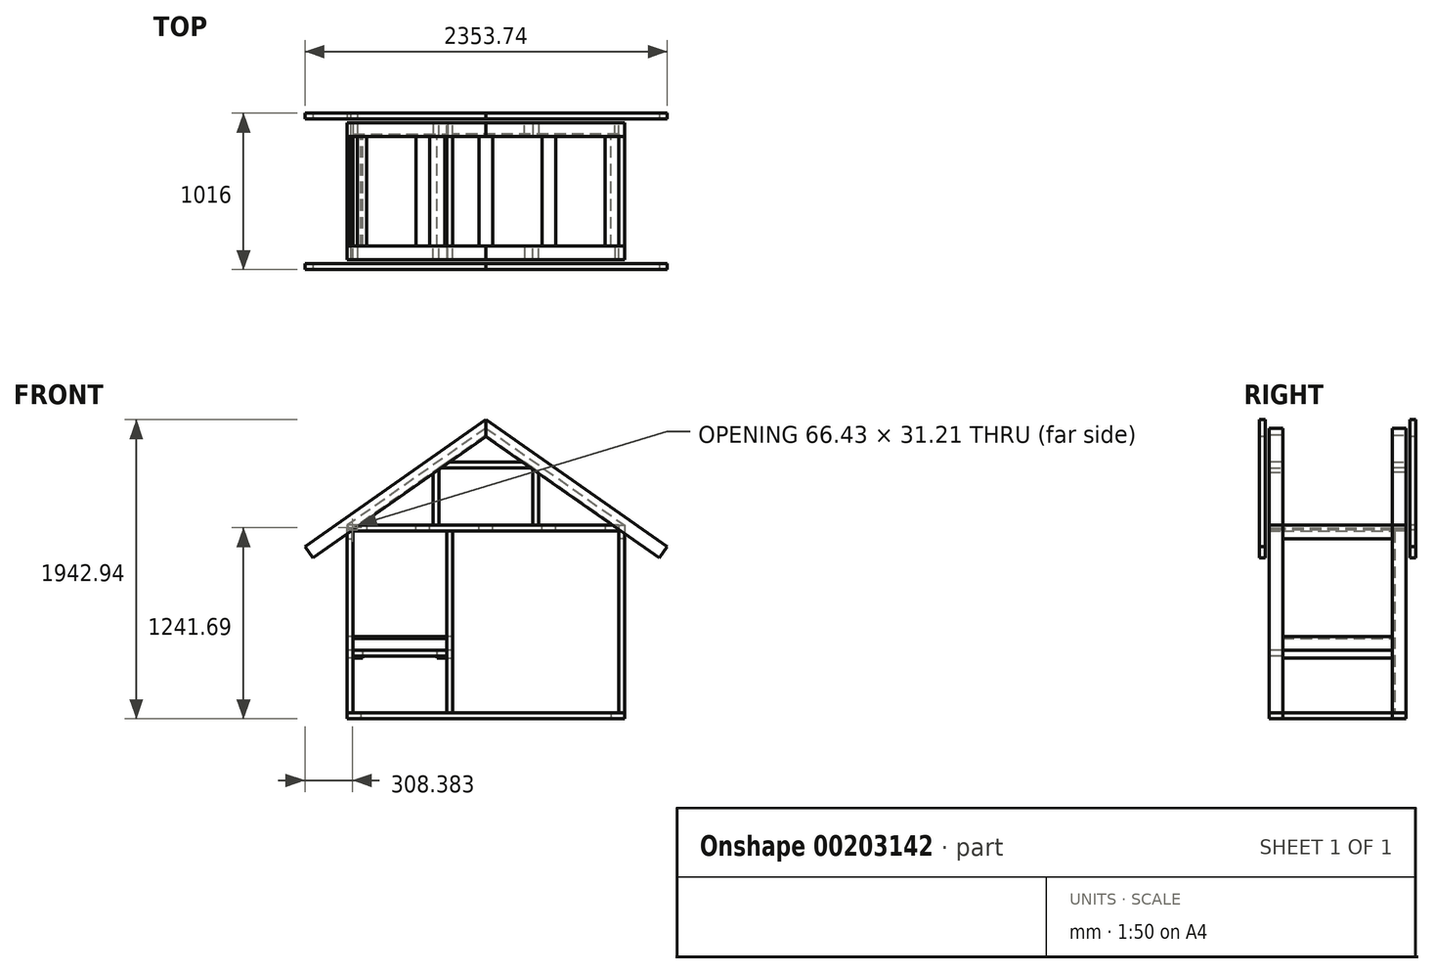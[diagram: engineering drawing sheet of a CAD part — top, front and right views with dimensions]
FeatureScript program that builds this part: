
annotation { "Feature Type Name" : "Feature", "Feature Type Description" : "" }
export const myFeature = defineFeature(function(context is Context, id is Id, definition is map)
    precondition{}
    {
        {
            var Q0;
            Q0=qCreatedBy(makeId("Top.planeOp"),FACE);
            var sketch = newSketch(context, id + "F0", { "sketchPlane" : qUnion([Q0])});
            skLineSegment(sketch, "E0.bottom", {"start": v(-901.7, 444.5) * mm, "end": v(-863.6, 444.5) * mm});
            skLineSegment(sketch, "E0.top", {"start": v(-901.7, 355.6) * mm, "end": v(-863.6, 355.6) * mm});
            skLineSegment(sketch, "E0.left", {"start": v(-901.7, 444.5) * mm, "end": v(-901.7, 355.6) * mm});
            skLineSegment(sketch, "E0.right", {"start": v(-863.6, 444.5) * mm, "end": v(-863.6, 355.6) * mm});
            skLineSegment(sketch, "E1.bottom", {"start": v(-901.7, -355.6) * mm, "end": v(-863.6, -355.6) * mm});
            skLineSegment(sketch, "E1.top", {"start": v(-901.7, -444.5) * mm, "end": v(-863.6, -444.5) * mm});
            skLineSegment(sketch, "E1.left", {"start": v(-901.7, -355.6) * mm, "end": v(-901.7, -444.5) * mm});
            skLineSegment(sketch, "E1.right", {"start": v(-863.6, -355.6) * mm, "end": v(-863.6, -444.5) * mm});
            skLineSegment(sketch, "E2.bottom", {"start": v(863.6, -444.5) * mm, "end": v(901.7, -444.5) * mm});
            skLineSegment(sketch, "E2.top", {"start": v(863.6, -355.6) * mm, "end": v(901.7, -355.6) * mm});
            skLineSegment(sketch, "E2.left", {"start": v(863.6, -444.5) * mm, "end": v(863.6, -355.6) * mm});
            skLineSegment(sketch, "E2.right", {"start": v(901.7, -444.5) * mm, "end": v(901.7, -355.6) * mm});
            skLineSegment(sketch, "E3.bottom", {"start": v(863.6, 355.6) * mm, "end": v(901.7, 355.6) * mm});
            skLineSegment(sketch, "E3.top", {"start": v(863.6, 444.5) * mm, "end": v(901.7, 444.5) * mm});
            skLineSegment(sketch, "E3.left", {"start": v(863.6, 355.6) * mm, "end": v(863.6, 444.5) * mm});
            skLineSegment(sketch, "E3.right", {"start": v(901.7, 355.6) * mm, "end": v(901.7, 444.5) * mm});
            skLineSegment(sketch, "E4", {"start": v(901.7, 444.5) * mm, "end": v(-901.7, -444.5) * mm, "construction": true});
            skPoint(sketch, "E5", {"position": v(0, 0) * mm});
            skSolve(sketch);
        }
        {
            var Q0;
            Q0 = qSketchRegion(id + "F0", true);
            extrude(context, id + "F1", {"entities" : qUnion([Q0]), "depth" : 1219.2 * mm});
        }
        {
            var Q0;
            Q0=makeQuery(id+"F1.opExtrude","SWEPT_FACE",FACE,{"disambiguationData":[OSD([sQuery(id+"F0.wireOp",EDGE,"E1.left")])]});
            var sketch = newSketch(context, id + "F2", { "sketchPlane" : qUnion([Q0])});
            skLineSegment(sketch, "E6.bottom", {"start": v(444.5, 0) * mm, "end": v(355.6, 0) * mm});
            skLineSegment(sketch, "E6.top", {"start": v(444.5, -38.1) * mm, "end": v(355.6, -38.1) * mm});
            skLineSegment(sketch, "E6.left", {"start": v(444.5, 0) * mm, "end": v(444.5, -38.1) * mm});
            skLineSegment(sketch, "E6.right", {"start": v(355.6, 0) * mm, "end": v(355.6, -38.1) * mm});
            skLineSegment(sketch, "E7.bottom", {"start": v(-355.6, 0) * mm, "end": v(-444.5, 0) * mm});
            skLineSegment(sketch, "E7.top", {"start": v(-355.6, -38.1) * mm, "end": v(-444.5, -38.1) * mm});
            skLineSegment(sketch, "E7.left", {"start": v(-355.6, 0) * mm, "end": v(-355.6, -38.1) * mm});
            skLineSegment(sketch, "E7.right", {"start": v(-444.5, 0) * mm, "end": v(-444.5, -38.1) * mm});
            skSolve(sketch);
        }
        {
            var Q0;
            Q0 = qSketchRegion(id + "F2", true);
            var Q1;
            Q1=makeQuery(id+"F1.opExtrude","SWEPT_FACE",FACE,{"disambiguationData":[OSD([sQuery(id+"F0.wireOp",EDGE,"E2.right")])]});
            extrude(context, id + "F3", {"entities" : qUnion([Q0]), "endBound" : BoundingType.UP_TO_SURFACE, "oppositeDirection" : true, "endBoundEntityFace" : qUnion([Q1]), "depth" : 25.4 * mm});
        }
        {
            var Q0;
            Q0=makeQuery(id+"F3.opExtrude","SWEPT_FACE",FACE,{"disambiguationData":[OSD([sQuery(id+"F2.wireOp",EDGE,"E7.left")])]});
            var sketch = newSketch(context, id + "F4", { "sketchPlane" : qUnion([Q0])});
            skLineSegment(sketch, "E8.bottom", {"start": v(-901.7, -38.1) * mm, "end": v(-812.8, -38.1) * mm});
            skLineSegment(sketch, "E8.top", {"start": v(-901.7, 0) * mm, "end": v(-812.8, 0) * mm});
            skLineSegment(sketch, "E8.left", {"start": v(-901.7, -38.1) * mm, "end": v(-901.7, 0) * mm});
            skLineSegment(sketch, "E8.right", {"start": v(-812.8, -38.1) * mm, "end": v(-812.8, 0) * mm});
            skLineSegment(sketch, "E9.bottom", {"start": v(901.7, -38.1) * mm, "end": v(812.8, -38.1) * mm});
            skLineSegment(sketch, "E9.top", {"start": v(901.7, 0) * mm, "end": v(812.8, 0) * mm});
            skLineSegment(sketch, "E9.left", {"start": v(901.7, -38.1) * mm, "end": v(901.7, 0) * mm});
            skLineSegment(sketch, "E9.right", {"start": v(812.8, -38.1) * mm, "end": v(812.8, 0) * mm});
            skSolve(sketch);
        }
        {
            var Q0;
            Q0 = qSketchRegion(id + "F4", true);
            var Q1;
            Q1=makeQuery(id+"F3.opExtrude","SWEPT_FACE",FACE,{"disambiguationData":[OSD([sQuery(id+"F2.wireOp",EDGE,"E6.right")])]});
            extrude(context, id + "F5", {"entities" : qUnion([Q0]), "endBound" : BoundingType.UP_TO_SURFACE, "endBoundEntityFace" : qUnion([Q1]), "depth" : 25.4 * mm});
        }
        {
            var Q0;
            Q0=makeQuery(id+"F1.opExtrude","SWEPT_FACE",FACE,{"disambiguationData":[OSD([sQuery(id+"F0.wireOp",EDGE,"E1.right")])]});
            var sketch = newSketch(context, id + "F6", { "sketchPlane" : qUnion([Q0])});
            skLineSegment(sketch, "E10.bottom", {"start": v(-444.5, 1219.2) * mm, "end": v(-355.6, 1219.2) * mm});
            skLineSegment(sketch, "E10.top", {"start": v(-444.5, 1181.1) * mm, "end": v(-355.6, 1181.1) * mm});
            skLineSegment(sketch, "E10.left", {"start": v(-444.5, 1219.2) * mm, "end": v(-444.5, 1181.1) * mm});
            skLineSegment(sketch, "E10.right", {"start": v(-355.6, 1219.2) * mm, "end": v(-355.6, 1181.1) * mm});
            skLineSegment(sketch, "E11.bottom", {"start": v(444.5, 1181.1) * mm, "end": v(355.6, 1181.1) * mm});
            skLineSegment(sketch, "E11.top", {"start": v(444.5, 1219.2) * mm, "end": v(355.6, 1219.2) * mm});
            skLineSegment(sketch, "E11.left", {"start": v(444.5, 1181.1) * mm, "end": v(444.5, 1219.2) * mm});
            skLineSegment(sketch, "E11.right", {"start": v(355.6, 1181.1) * mm, "end": v(355.6, 1219.2) * mm});
            skSolve(sketch);
        }
        {
            var Q0;
            Q0 = qSketchRegion(id + "F6", true);
            var Q1;
            Q1=makeQuery(id+"F1.opExtrude","SWEPT_FACE",FACE,{"disambiguationData":[OSD([sQuery(id+"F0.wireOp",EDGE,"E3.left")])]});
            extrude(context, id + "F7", {"entities" : qUnion([Q0]), "endBound" : BoundingType.UP_TO_SURFACE, "endBoundEntityFace" : qUnion([Q1]), "depth" : 25.4 * mm});
        }
        {
            var Q0;
            Q0=makeQuery(id+"F1.opExtrude","SWEPT_FACE",FACE,{"disambiguationData":[OSD([sQuery(id+"F0.wireOp",EDGE,"E0.top")])]});
            var sketch = newSketch(context, id + "F8", { "sketchPlane" : qUnion([Q0])});
            skLineSegment(sketch, "E12.bottom", {"start": v(-863.6, 1219.2) * mm, "end": v(-901.7, 1219.2) * mm});
            skLineSegment(sketch, "E12.top", {"start": v(-863.6, 1130.3) * mm, "end": v(-901.7, 1130.3) * mm});
            skLineSegment(sketch, "E12.left", {"start": v(-863.6, 1219.2) * mm, "end": v(-863.6, 1130.3) * mm});
            skLineSegment(sketch, "E12.right", {"start": v(-901.7, 1219.2) * mm, "end": v(-901.7, 1130.3) * mm});
            skLineSegment(sketch, "E13.bottom", {"start": v(863.6, 1130.3) * mm, "end": v(901.7, 1130.3) * mm});
            skLineSegment(sketch, "E13.top", {"start": v(863.6, 1219.2) * mm, "end": v(901.7, 1219.2) * mm});
            skLineSegment(sketch, "E13.left", {"start": v(863.6, 1130.3) * mm, "end": v(863.6, 1219.2) * mm});
            skLineSegment(sketch, "E13.right", {"start": v(901.7, 1130.3) * mm, "end": v(901.7, 1219.2) * mm});
            skSolve(sketch);
        }
        {
            var Q0;
            Q0 = qSketchRegion(id + "F8", true);
            var Q1;
            Q1=makeQuery(id+"F1.opExtrude","SWEPT_FACE",FACE,{"disambiguationData":[OSD([sQuery(id+"F0.wireOp",EDGE,"E1.bottom")])]});
            extrude(context, id + "F9", {"entities" : qUnion([Q0]), "endBound" : BoundingType.UP_TO_SURFACE, "endBoundEntityFace" : qUnion([Q1]), "depth" : 25.4 * mm});
        }
        {
            var Q0;
            Q0=makeQuery(id+"F9.opExtrude","SWEPT_EDGE",EDGE,{"disambiguationData":[OSD([sQuery(id+"F8.wireOp",EDGE,"E12.bottom"),sQuery(id+"F8.wireOp",EDGE,"E12.right")])]});
            cPlane(context, id + "F10", {"entities" : qUnion([Q0]), "cplaneType" : CPlaneType.LINE_ANGLE, "offset" : 25.4 * mm, "angle" : 55 * degree, "width" : 152.4 * mm, "height" : 152.4 * mm});
        }
        {
            var Q0;
            Q0=qCreatedBy(id+"F10.planeOp",FACE);
            var sketch = newSketch(context, id + "F11", { "sketchPlane" : qUnion([Q0])});
            skLineSegment(sketch, "E14.bottom", {"start": v(-469.9, 1471.45) * mm, "end": v(-508, 1471.45) * mm});
            skLineSegment(sketch, "E14.top", {"start": v(-469.9, 1560.35) * mm, "end": v(-508, 1560.35) * mm});
            skLineSegment(sketch, "E14.left", {"start": v(-469.9, 1471.45) * mm, "end": v(-469.9, 1560.35) * mm});
            skLineSegment(sketch, "E14.right", {"start": v(-508, 1471.45) * mm, "end": v(-508, 1560.35) * mm});
            skPoint(sketch, "E15", {"position": v(-469.9, 1515.9) * mm});
            skLineSegment(sketch, "E16", {"start": v(-469.9, 1515.9) * mm, "end": v(-444.5, 1515.9) * mm, "construction": true});
            skLineSegment(sketch, "E17.bottom", {"start": v(508, 1471.45) * mm, "end": v(469.9, 1471.45) * mm});
            skLineSegment(sketch, "E17.top", {"start": v(508, 1560.35) * mm, "end": v(469.9, 1560.35) * mm});
            skLineSegment(sketch, "E17.left", {"start": v(508, 1471.45) * mm, "end": v(508, 1560.35) * mm});
            skLineSegment(sketch, "E17.right", {"start": v(469.9, 1471.45) * mm, "end": v(469.9, 1560.35) * mm});
            skSolve(sketch);
        }
        {
            var Q0;
            Q0 = qSketchRegion(id + "F11", true);
            var Q1;
            Q1=qCreatedBy(makeId("Right.planeOp"),FACE);
            extrude(context, id + "F12", {"entities" : qUnion([Q0]), "endBound" : BoundingType.UP_TO_SURFACE, "endBoundEntityFace" : qUnion([Q1]), "depth" : 914.4 * mm, "hasSecondDirection" : true, "secondDirectionOppositeDirection" : true, "secondDirectionDepth" : 304.8 * mm});
        }
        {
            var Q0;
            Q0=makeQuery(id+"F12.opExtrude","SWEPT_BODY",BODY,{"disambiguationData":[OSD([sQuery(id+"F11.wireOp",EDGE,"E14.bottom"),sQuery(id+"F11.wireOp",EDGE,"E14.top"),sQuery(id+"F11.wireOp",EDGE,"E14.left"),sQuery(id+"F11.wireOp",EDGE,"E14.right")])]});
            var Q1;
            Q1=makeQuery(id+"F12.opExtrude","SWEPT_BODY",BODY,{"disambiguationData":[OSD([sQuery(id+"F11.wireOp",EDGE,"E17.bottom"),sQuery(id+"F11.wireOp",EDGE,"E17.top"),sQuery(id+"F11.wireOp",EDGE,"E17.left"),sQuery(id+"F11.wireOp",EDGE,"E17.right")])]});
            var Q2;
            Q2=qCreatedBy(makeId("Right.planeOp"),FACE);
            mirror(context, id + "F13", {"entities" : qUnion([Q0, Q1]), "mirrorPlane" : qUnion([Q2])});
        }
        {
            var Q0;
            Q0=makeQuery(id+"F3.opExtrude","SWEPT_FACE",FACE,{"disambiguationData":[OSD([sQuery(id+"F2.wireOp",EDGE,"E6.bottom")])]});
            var sketch = newSketch(context, id + "F14", { "sketchPlane" : qUnion([Q0])});
            skLineSegment(sketch, "E18.bottom", {"start": v(-254, -444.5) * mm, "end": v(-215.9, -444.5) * mm});
            skLineSegment(sketch, "E18.top", {"start": v(-254, -355.6) * mm, "end": v(-215.9, -355.6) * mm});
            skLineSegment(sketch, "E18.left", {"start": v(-254, -444.5) * mm, "end": v(-254, -355.6) * mm});
            skLineSegment(sketch, "E18.right", {"start": v(-215.9, -444.5) * mm, "end": v(-215.9, -355.6) * mm});
            skLineSegment(sketch, "E19.bottom", {"start": v(-215.9, 355.6) * mm, "end": v(-254, 355.6) * mm});
            skLineSegment(sketch, "E19.top", {"start": v(-215.9, 444.5) * mm, "end": v(-254, 444.5) * mm});
            skLineSegment(sketch, "E19.left", {"start": v(-215.9, 355.6) * mm, "end": v(-215.9, 444.5) * mm});
            skLineSegment(sketch, "E19.right", {"start": v(-254, 355.6) * mm, "end": v(-254, 444.5) * mm});
            skSolve(sketch);
        }
        {
            var Q0;
            Q0 = qSketchRegion(id + "F14", true);
            var Q1;
            Q1=makeQuery(id+"F7.opExtrude","SWEPT_FACE",FACE,{"disambiguationData":[OSD([sQuery(id+"F6.wireOp",EDGE,"E10.top")])]});
            var Q2;
            Q2=makeQuery(id+"F7.opExtrude","SWEPT_BODY",BODY,{"disambiguationData":[OSD([sQuery(id+"F6.wireOp",EDGE,"E10.bottom"),sQuery(id+"F6.wireOp",EDGE,"E10.top"),sQuery(id+"F6.wireOp",EDGE,"E10.left"),sQuery(id+"F6.wireOp",EDGE,"E10.right")])]});
            extrude(context, id + "F15", {"entities" : qUnion([Q0]), "endBound" : BoundingType.UP_TO_SURFACE, "endBoundEntityFace" : qUnion([Q1]), "endBoundEntityBody" : qUnion([Q2]), "depth" : 25.4 * mm});
        }
        {
            var Q0;
            Q0=makeQuery(id+"F1.opExtrude","SWEPT_FACE",FACE,{"disambiguationData":[OSD([sQuery(id+"F0.wireOp",EDGE,"E0.top")])]});
            var sketch = newSketch(context, id + "F16", { "sketchPlane" : qUnion([Q0])});
            skLineSegment(sketch, "E20.bottom", {"start": v(-901.7, 406.4) * mm, "end": v(-863.6, 406.4) * mm});
            skLineSegment(sketch, "E20.top", {"start": v(-901.7, 495.3) * mm, "end": v(-863.6, 495.3) * mm});
            skLineSegment(sketch, "E20.left", {"start": v(-901.7, 406.4) * mm, "end": v(-901.7, 495.3) * mm});
            skLineSegment(sketch, "E20.right", {"start": v(-863.6, 406.4) * mm, "end": v(-863.6, 495.3) * mm});
            skLineSegment(sketch, "E21.bottom", {"start": v(-254, 406.4) * mm, "end": v(-215.9, 406.4) * mm});
            skLineSegment(sketch, "E21.top", {"start": v(-254, 495.3) * mm, "end": v(-215.9, 495.3) * mm});
            skLineSegment(sketch, "E21.left", {"start": v(-254, 406.4) * mm, "end": v(-254, 495.3) * mm});
            skLineSegment(sketch, "E21.right", {"start": v(-215.9, 406.4) * mm, "end": v(-215.9, 495.3) * mm});
            skSolve(sketch);
        }
        {
            var Q0;
            Q0 = qSketchRegion(id + "F16", true);
            var Q1;
            Q1=makeQuery(id+"F1.opExtrude","SWEPT_FACE",FACE,{"disambiguationData":[OSD([sQuery(id+"F0.wireOp",EDGE,"E1.bottom")])]});
            extrude(context, id + "F17", {"entities" : qUnion([Q0]), "endBound" : BoundingType.UP_TO_SURFACE, "endBoundEntityFace" : qUnion([Q1]), "depth" : 25.4 * mm});
        }
        {
            var Q0;
            Q0=makeQuery(id+"F1.opExtrude","SWEPT_FACE",FACE,{"disambiguationData":[OSD([sQuery(id+"F0.wireOp",EDGE,"E0.top")])]});
            var sketch = newSketch(context, id + "F18", { "sketchPlane" : qUnion([Q0])});
            skLineSegment(sketch, "E22.bottom", {"start": v(-901.7, 406.4) * mm, "end": v(-800.1, 406.4) * mm});
            skLineSegment(sketch, "E22.top", {"start": v(-901.7, 355.6) * mm, "end": v(-800.1, 355.6) * mm});
            skLineSegment(sketch, "E22.left", {"start": v(-901.7, 406.4) * mm, "end": v(-901.7, 355.6) * mm});
            skLineSegment(sketch, "E22.right", {"start": v(-800.1, 406.4) * mm, "end": v(-800.1, 355.6) * mm});
            skLineSegment(sketch, "E23.bottom", {"start": v(-215.9, 406.4) * mm, "end": v(-317.5, 406.4) * mm});
            skLineSegment(sketch, "E23.top", {"start": v(-215.9, 355.6) * mm, "end": v(-317.5, 355.6) * mm});
            skLineSegment(sketch, "E23.left", {"start": v(-215.9, 406.4) * mm, "end": v(-215.9, 355.6) * mm});
            skLineSegment(sketch, "E23.right", {"start": v(-317.5, 406.4) * mm, "end": v(-317.5, 355.6) * mm});
            skSolve(sketch);
        }
        {
            var Q0;
            Q0 = qSketchRegion(id + "F18", true);
            var Q1;
            Q1=makeQuery(id+"F1.opExtrude","SWEPT_FACE",FACE,{"disambiguationData":[OSD([sQuery(id+"F0.wireOp",EDGE,"E1.bottom")])]});
            extrude(context, id + "F19", {"entities" : qUnion([Q0]), "endBound" : BoundingType.UP_TO_SURFACE, "endBoundEntityFace" : qUnion([Q1]), "depth" : 25.4 * mm});
        }
        {
            var Q0;
            Q0=makeQuery(id+"F1.opExtrude","SWEPT_FACE",FACE,{"disambiguationData":[OSD([sQuery(id+"F0.wireOp",EDGE,"E1.right")])]});
            var sketch = newSketch(context, id + "F20", { "sketchPlane" : qUnion([Q0])});
            skLineSegment(sketch, "E24.bottom", {"start": v(-444.5, 368.3) * mm, "end": v(-355.6, 368.3) * mm});
            skLineSegment(sketch, "E24.top", {"start": v(-444.5, 406.4) * mm, "end": v(-355.6, 406.4) * mm});
            skLineSegment(sketch, "E24.left", {"start": v(-444.5, 368.3) * mm, "end": v(-444.5, 406.4) * mm});
            skLineSegment(sketch, "E24.right", {"start": v(-355.6, 368.3) * mm, "end": v(-355.6, 406.4) * mm});
            skSolve(sketch);
        }
        {
            var Q0;
            Q0 = qSketchRegion(id + "F20", true);
            var Q1;
            Q1=makeQuery(id+"F15.opExtrude","SWEPT_FACE",FACE,{"disambiguationData":[OSD([sQuery(id+"F14.wireOp",EDGE,"E18.left")])]});
            extrude(context, id + "F21", {"entities" : qUnion([Q0]), "endBound" : BoundingType.UP_TO_SURFACE, "endBoundEntityFace" : qUnion([Q1]), "depth" : 25.4 * mm});
        }
        {
            var Q0;
            Q0=makeQuery(id+"F17.opExtrude","SWEPT_FACE",FACE,{"disambiguationData":[OSD([sQuery(id+"F16.wireOp",EDGE,"E20.top")])]});
            var sketch = newSketch(context, id + "F22", { "sketchPlane" : qUnion([Q0])});
            skLineSegment(sketch, "E25.bottom", {"start": v(-863.6, 355.6) * mm, "end": v(-266.7, 355.6) * mm});
            skLineSegment(sketch, "E25.top", {"start": v(-863.6, -355.6) * mm, "end": v(-266.7, -355.6) * mm});
            skLineSegment(sketch, "E25.left", {"start": v(-863.6, 355.6) * mm, "end": v(-863.6, -355.6) * mm});
            skLineSegment(sketch, "E25.right", {"start": v(-266.7, 355.6) * mm, "end": v(-266.7, -355.6) * mm});
            skSolve(sketch);
        }
        {
            var Q0;
            Q0=makeQuery(id+"F22.imprint","IMPRINT",FACE,{"disambiguationData":[TD([[makeQuery(id+"F22.imprint","IMPRINT",EDGE,{"derivedFrom":sQuery(id+"F22.wireOp",EDGE,"E25.bottom")}),-1.0]])]});
            extrude(context, id + "F23", {"entities" : qUnion([Q0]), "oppositeDirection" : true, "depth" : 12.7 * mm});
        }
        {
            var Q0;
            Q0=makeQuery(id+"F7.opExtrude","SWEPT_FACE",FACE,{"disambiguationData":[OSD([sQuery(id+"F6.wireOp",EDGE,"E11.right")])]});
            var sketch = newSketch(context, id + "F24", { "sketchPlane" : qUnion([Q0])});
            skLineSegment(sketch, "E26.bottom", {"start": v(-863.6, 1181.1) * mm, "end": v(-774.7, 1181.1) * mm});
            skLineSegment(sketch, "E26.top", {"start": v(-863.6, 1219.2) * mm, "end": v(-774.7, 1219.2) * mm});
            skLineSegment(sketch, "E26.left", {"start": v(-863.6, 1181.1) * mm, "end": v(-863.6, 1219.2) * mm});
            skLineSegment(sketch, "E26.right", {"start": v(-774.7, 1181.1) * mm, "end": v(-774.7, 1219.2) * mm});
            skLineSegment(sketch, "E27.bottom", {"start": v(863.6, 1181.1) * mm, "end": v(774.7, 1181.1) * mm});
            skLineSegment(sketch, "E27.top", {"start": v(863.6, 1219.2) * mm, "end": v(774.7, 1219.2) * mm});
            skLineSegment(sketch, "E27.left", {"start": v(863.6, 1181.1) * mm, "end": v(863.6, 1219.2) * mm});
            skLineSegment(sketch, "E27.right", {"start": v(774.7, 1181.1) * mm, "end": v(774.7, 1219.2) * mm});
            skLineSegment(sketch, "E28.bottom", {"start": v(-44.45, 1219.2) * mm, "end": v(44.45, 1219.2) * mm});
            skLineSegment(sketch, "E28.top", {"start": v(-44.45, 1181.1) * mm, "end": v(44.45, 1181.1) * mm});
            skLineSegment(sketch, "E28.left", {"start": v(-44.45, 1219.2) * mm, "end": v(-44.45, 1181.1) * mm});
            skLineSegment(sketch, "E28.right", {"start": v(44.45, 1219.2) * mm, "end": v(44.45, 1181.1) * mm});
            skLineSegment(sketch, "E29.bottom", {"start": v(365.12, 1219.2) * mm, "end": v(454.02, 1219.2) * mm});
            skLineSegment(sketch, "E29.top", {"start": v(365.12, 1181.1) * mm, "end": v(454.02, 1181.1) * mm});
            skLineSegment(sketch, "E29.left", {"start": v(365.12, 1219.2) * mm, "end": v(365.12, 1181.1) * mm});
            skLineSegment(sketch, "E29.right", {"start": v(454.02, 1219.2) * mm, "end": v(454.02, 1181.1) * mm});
            skLineSegment(sketch, "E30.bottom", {"start": v(-454.03, 1219.2) * mm, "end": v(-365.12, 1219.2) * mm});
            skLineSegment(sketch, "E30.top", {"start": v(-454.02, 1181.1) * mm, "end": v(-365.12, 1181.1) * mm});
            skLineSegment(sketch, "E30.left", {"start": v(-454.02, 1219.2) * mm, "end": v(-454.02, 1181.1) * mm});
            skLineSegment(sketch, "E30.right", {"start": v(-365.12, 1219.2) * mm, "end": v(-365.12, 1181.1) * mm});
            skPoint(sketch, "E31", {"position": v(-409.57, 1181.1) * mm});
            skSolve(sketch);
        }
        {
            var Q0;
            Q0 = qSketchRegion(id + "F24", true);
            var Q1;
            Q1=makeQuery(id+"F7.opExtrude","SWEPT_FACE",FACE,{"disambiguationData":[OSD([sQuery(id+"F6.wireOp",EDGE,"E10.right")])]});
            extrude(context, id + "F25", {"entities" : qUnion([Q0]), "endBound" : BoundingType.UP_TO_SURFACE, "endBoundEntityFace" : qUnion([Q1]), "depth" : 25.4 * mm});
        }
        {
            var Q0;
            Q0=makeQuery(id+"F15.opExtrude","SWEPT_FACE",FACE,{"disambiguationData":[OSD([sQuery(id+"F14.wireOp",EDGE,"E19.left")])]});
            var sketch = newSketch(context, id + "F26", { "sketchPlane" : qUnion([Q0])});
            skLineSegment(sketch, "E32.bottom", {"start": v(355.6, 0) * mm, "end": v(371.48, 0) * mm});
            skLineSegment(sketch, "E32.top", {"start": v(355.6, 1181.1) * mm, "end": v(371.47, 1181.1) * mm});
            skLineSegment(sketch, "E32.left", {"start": v(355.6, 0) * mm, "end": v(355.6, 1181.1) * mm});
            skLineSegment(sketch, "E32.right", {"start": v(371.48, 0) * mm, "end": v(371.47, 1181.1) * mm});
            skSolve(sketch);
        }
        {
            var Q0;
            Q0 = qSketchRegion(id + "F26", true);
            var Q1;
            Q1=makeQuery(id+"F1.opExtrude","SWEPT_FACE",FACE,{"disambiguationData":[OSD([sQuery(id+"F0.wireOp",EDGE,"E3.left")])]});
            extrude(context, id + "F27", {"entities" : qUnion([Q0]), "endBound" : BoundingType.UP_TO_SURFACE, "endBoundEntityFace" : qUnion([Q1]), "depth" : 25.4 * mm});
        }
        {
            var Q0;
            Q0=makeQuery(id+"F15.opExtrude","SWEPT_FACE",FACE,{"disambiguationData":[OSD([sQuery(id+"F14.wireOp",EDGE,"E19.right")])]});
            var sketch = newSketch(context, id + "F28", { "sketchPlane" : qUnion([Q0])});
            skLineSegment(sketch, "E33.bottom", {"start": v(-355.6, 0) * mm, "end": v(-371.48, 0) * mm});
            skLineSegment(sketch, "E33.top", {"start": v(-355.6, 1181.1) * mm, "end": v(-371.48, 1181.1) * mm});
            skLineSegment(sketch, "E33.left", {"start": v(-355.6, 0) * mm, "end": v(-355.6, 1181.1) * mm});
            skLineSegment(sketch, "E33.right", {"start": v(-371.48, 0) * mm, "end": v(-371.48, 1181.1) * mm});
            skSolve(sketch);
        }
        {
            var Q0;
            Q0 = qSketchRegion(id + "F28", true);
            var Q1;
            Q1=makeQuery(id+"F1.opExtrude","SWEPT_FACE",FACE,{"disambiguationData":[OSD([sQuery(id+"F0.wireOp",EDGE,"E0.right")])]});
            extrude(context, id + "F29", {"entities" : qUnion([Q0]), "endBound" : BoundingType.UP_TO_SURFACE, "endBoundEntityFace" : qUnion([Q1]), "depth" : 25.4 * mm});
        }
        {
            var Q0;
            Q0=qCreatedBy(id+"F10.planeOp",FACE);
            var sketch = newSketch(context, id + "F30", { "sketchPlane" : qUnion([Q0])});
            skLineSegment(sketch, "E34.bottom", {"start": v(-355.6, 1515.9) * mm, "end": v(-444.5, 1515.9) * mm});
            skLineSegment(sketch, "E34.top", {"start": v(-355.6, 1477.8) * mm, "end": v(-444.5, 1477.8) * mm});
            skLineSegment(sketch, "E34.left", {"start": v(-355.6, 1515.9) * mm, "end": v(-355.6, 1477.8) * mm});
            skLineSegment(sketch, "E34.right", {"start": v(-444.5, 1515.9) * mm, "end": v(-444.5, 1477.8) * mm});
            skSolve(sketch);
        }
        {
            var Q0;
            Q0 = qSketchRegion(id + "F30", true);
            var Q1;
            Q1=qCreatedBy(makeId("Right.planeOp"),FACE);
            extrude(context, id + "F31", {"entities" : qUnion([Q0]), "endBound" : BoundingType.UP_TO_SURFACE, "endBoundEntityFace" : qUnion([Q1]), "depth" : 1059.18 * mm});
        }
        {
            var Q0;
            Q0=makeQuery(id+"F31.opExtrude","SWEPT_FACE",FACE,{"disambiguationData":[OSD([sQuery(id+"F30.wireOp",EDGE,"E34.right")])]});
            var sketch = newSketch(context, id + "F32", { "sketchPlane" : qUnion([Q0])});
            skLineSegment(sketch, "E35", {"start": v(-901.7, 1219.2) * mm, "end": v(-835.27, 1219.2) * mm});
            skLineSegment(sketch, "E36", {"start": v(-835.27, 1219.2) * mm, "end": v(-879.85, 1188) * mm});
            skLineSegment(sketch, "E37", {"start": v(-879.85, 1188) * mm, "end": v(-901.7, 1219.2) * mm});
            skSolve(sketch);
        }
        {
            var Q0;
            Q0 = qSketchRegion(id + "F32", true);
            extrude(context, id + "F33", {"entities" : qUnion([Q0]), "operationType" : NewBodyOperationType.REMOVE, "endBound" : BoundingType.THROUGH_ALL, "oppositeDirection" : true, "depth" : 25.4 * mm});
        }
        {
            var Q0;
            Q0=makeQuery(id+"F7.opExtrude","SWEPT_FACE",FACE,{"disambiguationData":[OSD([sQuery(id+"F6.wireOp",EDGE,"E10.bottom")])]});
            var sketch = newSketch(context, id + "F34", { "sketchPlane" : qUnion([Q0])});
            skLineSegment(sketch, "E38.bottom", {"start": v(-342.9, -355.6) * mm, "end": v(-304.8, -355.6) * mm});
            skLineSegment(sketch, "E38.top", {"start": v(-342.9, -444.5) * mm, "end": v(-304.8, -444.5) * mm});
            skLineSegment(sketch, "E38.left", {"start": v(-342.9, -355.6) * mm, "end": v(-342.9, -444.5) * mm});
            skLineSegment(sketch, "E38.right", {"start": v(-304.8, -355.6) * mm, "end": v(-304.8, -444.5) * mm});
            skLineSegment(sketch, "E39", {"start": v(0, -355.6) * mm, "end": v(0, -444.5) * mm, "construction": true});
            skLineSegment(sketch, "E40.bottom", {"start": v(304.8, -355.6) * mm, "end": v(342.9, -355.6) * mm, "construction": true});
            skLineSegment(sketch, "E40.top", {"start": v(304.8, -444.5) * mm, "end": v(342.9, -444.5) * mm, "construction": true});
            skLineSegment(sketch, "E40.left", {"start": v(304.8, -355.6) * mm, "end": v(304.8, -444.5) * mm, "construction": true});
            skLineSegment(sketch, "E40.right", {"start": v(342.9, -355.6) * mm, "end": v(342.9, -444.5) * mm, "construction": true});
            skSolve(sketch);
        }
        {
            var Q0;
            Q0 = qSketchRegion(id + "F34", true);
            var Q1;
            Q1=makeQuery(id+"F31.opExtrude","SWEPT_FACE",FACE,{"disambiguationData":[OSD([sQuery(id+"F30.wireOp",EDGE,"E34.top")])]});
            extrude(context, id + "F35", {"entities" : qUnion([Q0]), "endBound" : BoundingType.UP_TO_SURFACE, "endBoundEntityFace" : qUnion([Q1]), "depth" : 304.8 * mm});
        }
        {
            var Q0;
            Q0=makeQuery(id+"F31.opExtrude","SWEPT_BODY",BODY,{"disambiguationData":[OSD([sQuery(id+"F30.wireOp",EDGE,"E34.bottom"),sQuery(id+"F30.wireOp",EDGE,"E34.top"),sQuery(id+"F30.wireOp",EDGE,"E34.left"),sQuery(id+"F30.wireOp",EDGE,"E34.right")])]});
            var Q1;
            Q1=makeQuery(id+"F35.opExtrude","SWEPT_BODY",BODY,{"disambiguationData":[OSD([sQuery(id+"F34.wireOp",EDGE,"E38.bottom"),sQuery(id+"F34.wireOp",EDGE,"E38.top"),sQuery(id+"F34.wireOp",EDGE,"E38.left"),sQuery(id+"F34.wireOp",EDGE,"E38.right")])]});
            var Q2;
            Q2=qCreatedBy(makeId("Front.planeOp"),FACE);
            mirror(context, id + "F36", {"entities" : qUnion([Q0, Q1]), "mirrorPlane" : qUnion([Q2])});
        }
        {
            var Q0;
            Q0=makeQuery(id+"F36.opPattern","COPY",BODY,{"derivedFrom":makeQuery(id+"F35.opExtrude","SWEPT_BODY",BODY,{"disambiguationData":[OSD([sQuery(id+"F34.wireOp",EDGE,"E38.bottom"),sQuery(id+"F34.wireOp",EDGE,"E38.top"),sQuery(id+"F34.wireOp",EDGE,"E38.left"),sQuery(id+"F34.wireOp",EDGE,"E38.right")])]}),"instanceName":"1"});
            var Q1;
            Q1=makeQuery(id+"F36.opPattern","COPY",BODY,{"derivedFrom":makeQuery(id+"F31.opExtrude","SWEPT_BODY",BODY,{"disambiguationData":[OSD([sQuery(id+"F30.wireOp",EDGE,"E34.bottom"),sQuery(id+"F30.wireOp",EDGE,"E34.top"),sQuery(id+"F30.wireOp",EDGE,"E34.left"),sQuery(id+"F30.wireOp",EDGE,"E34.right")])]}),"instanceName":"1"});
            var Q2;
            Q2=makeQuery(id+"F35.opExtrude","SWEPT_BODY",BODY,{"disambiguationData":[OSD([sQuery(id+"F34.wireOp",EDGE,"E38.bottom"),sQuery(id+"F34.wireOp",EDGE,"E38.top"),sQuery(id+"F34.wireOp",EDGE,"E38.left"),sQuery(id+"F34.wireOp",EDGE,"E38.right")])]});
            var Q3;
            Q3=makeQuery(id+"F31.opExtrude","SWEPT_BODY",BODY,{"disambiguationData":[OSD([sQuery(id+"F30.wireOp",EDGE,"E34.bottom"),sQuery(id+"F30.wireOp",EDGE,"E34.top"),sQuery(id+"F30.wireOp",EDGE,"E34.left"),sQuery(id+"F30.wireOp",EDGE,"E34.right")])]});
            var Q4;
            Q4=qCreatedBy(makeId("Right.planeOp"),FACE);
            mirror(context, id + "F37", {"entities" : qUnion([Q0, Q1, Q2, Q3]), "mirrorPlane" : qUnion([Q4])});
        }
        {
            var Q0;
            Q0=qCreatedBy(makeId("Right.planeOp"),FACE);
            var sketch = newSketch(context, id + "F38", { "sketchPlane" : qUnion([Q0])});
            skLineSegment(sketch, "E41.0.0", {"start": v(-355.6, 1590.64) * mm, "end": v(-444.5, 1590.64) * mm, "construction": true});
            skLineSegment(sketch, "E41.0.1", {"start": v(-444.5, 1590.64) * mm, "end": v(-444.5, 1219.2) * mm, "construction": true});
            skLineSegment(sketch, "E41.0.2", {"start": v(-444.5, 1219.2) * mm, "end": v(-355.6, 1219.2) * mm, "construction": true});
            skLineSegment(sketch, "E41.0.3", {"start": v(-355.6, 1219.2) * mm, "end": v(-355.6, 1590.64) * mm, "construction": true});
            skLineSegment(sketch, "E42.bottom", {"start": v(-444.5, 1590.64) * mm, "end": v(-355.6, 1590.64) * mm});
            skLineSegment(sketch, "E42.top", {"start": v(-444.5, 1628.74) * mm, "end": v(-355.6, 1628.74) * mm});
            skLineSegment(sketch, "E42.left", {"start": v(-444.5, 1590.64) * mm, "end": v(-444.5, 1628.74) * mm});
            skLineSegment(sketch, "E42.right", {"start": v(-355.6, 1590.64) * mm, "end": v(-355.6, 1628.74) * mm});
            skLineSegment(sketch, "E43.0.0", {"start": v(444.5, 1590.64) * mm, "end": v(355.6, 1590.64) * mm, "construction": true});
            skLineSegment(sketch, "E43.0.1", {"start": v(355.6, 1590.64) * mm, "end": v(355.6, 1219.2) * mm, "construction": true});
            skLineSegment(sketch, "E43.0.2", {"start": v(355.6, 1219.2) * mm, "end": v(444.5, 1219.2) * mm, "construction": true});
            skLineSegment(sketch, "E43.0.3", {"start": v(444.5, 1219.2) * mm, "end": v(444.5, 1590.64) * mm, "construction": true});
            skLineSegment(sketch, "E44.bottom", {"start": v(355.6, 1590.64) * mm, "end": v(444.5, 1590.64) * mm});
            skLineSegment(sketch, "E44.top", {"start": v(355.6, 1590.64) * mm, "end": v(444.5, 1590.64) * mm});
            skLineSegment(sketch, "E44.left", {"start": v(355.6, 1590.64) * mm, "end": v(355.6, 1590.64) * mm});
            skLineSegment(sketch, "E44.right", {"start": v(444.5, 1590.64) * mm, "end": v(444.5, 1590.64) * mm});
            skLineSegment(sketch, "E45.bottom", {"start": v(444.5, 1628.74) * mm, "end": v(355.6, 1628.74) * mm});
            skLineSegment(sketch, "E45.top", {"start": v(444.5, 1590.64) * mm, "end": v(355.6, 1590.64) * mm});
            skLineSegment(sketch, "E45.left", {"start": v(444.5, 1628.74) * mm, "end": v(444.5, 1590.64) * mm});
            skLineSegment(sketch, "E45.right", {"start": v(355.6, 1628.74) * mm, "end": v(355.6, 1590.64) * mm});
            skSolve(sketch);
        }
        {
            var Q0;
            Q0=makeQuery(id+"F38.imprint","IMPRINT",FACE,{"disambiguationData":[TD([[makeQuery(id+"F38.imprint","IMPRINT",EDGE,{"derivedFrom":sQuery(id+"F38.wireOp",EDGE,"E42.bottom")}),1.0]])]});
            var Q1;
            Q1=makeQuery(id+"F38.imprint","IMPRINT",FACE,{"disambiguationData":[TD([[makeQuery(id+"F38.imprint","IMPRINT",EDGE,{"derivedFrom":sQuery(id+"F38.wireOp",EDGE,"E45.bottom")}),1.0]])]});
            extrude(context, id + "F39", {"entities" : qUnion([Q0, Q1]), "endBound" : BoundingType.UP_TO_NEXT, "depth" : 25.4 * mm, "hasSecondDirection" : true, "secondDirectionBound" : SecondDirectionBoundingType.UP_TO_NEXT, "secondDirectionOppositeDirection" : true, "secondDirectionDepth" : 25.4 * mm});
        }
    });
